# Revit family: SCCT-G
name_source: partatom
category: Lighting Fixtures
revit_build: Autodesk Revit 2014 (Build: 20130308_1515(x64)
units: mm (PartAtom-declared; Revit-internal decimal feet)

## types (3) — shared parameters
Apparent Load = 40 VA
Backbox = Hubbell - White
Color Filter = 16777215
Default Elevation = 48"
Description = LCAT provides both design and value with an architectural appearance, LED technology to reduce maintenance and a wide range of options for classrooms, offices, retail and health care applications
Dimming Lamp Color Temperature Shift = <None>
Emit Shape Visible in Rendering = No
Lamp = LED lamp
Light Bulb = Hubbell - White Glass
Manufacturer = Columbia Lighting
Model = SCCT-G
Photometric Web File = generic
Product Documentation Link = https://hubbellcdn.com
Product Page URL = https://www.hubbell.com
Tilt Angle = 60.00°
URL = https://www.hubbell.com
Voltage = 120 V
Warranty = Five-year warranty
Wattage Comments = 40-80 W

## per-type parameters (varying)
| type | Emit from Rectangle Length | Emit from Rectangle Width | Load Classification | Row Length | Width | zz Length |
| SCCT-G-14 | 48" | 12" | Lighting | 48" | 12" | 47" |
| SCCT-G-22 | 24" | 24" | Other | 24" | 24" | 23" |
| SCCT-G-24 | 48" | 25" | Other | 48" | 25" | 47" |

## geometry (parser evidence)
native form markers: Sweep x3
no freeform markers — native parametric forms only
